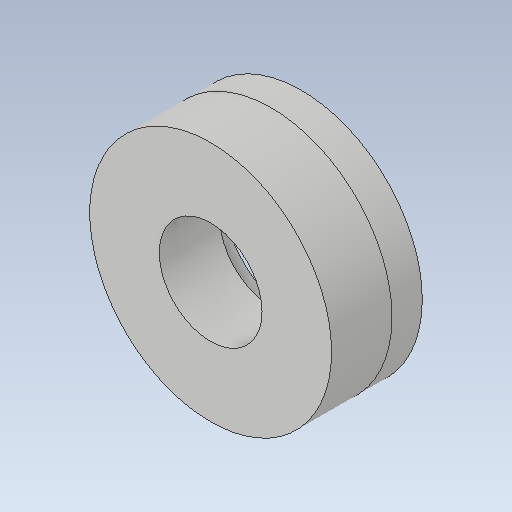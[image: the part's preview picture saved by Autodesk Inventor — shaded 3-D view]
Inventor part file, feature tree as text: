
AUTODESK INVENTOR PART (.ipt)
format: ipt  version: 2020 (Build 240168000, 168)  size: 116,736 bytes
history: native  units: mm
features: other x2, extrude x2, sketch x2
ambient origin geometry x8: Origin, YZ Plane, XZ Plane, XY Plane, X Axis, Y Axis, Z Axis, Center Point
bodies: Body1 (feature_tree), Body2 (feature_tree)
feature tree (6):
  other  "Твердое тело1"
  extrude  "Выдавливание1"  Depth=40.0mm
  extrude  "Выдавливание2"  Depth=26.9mm
  sketch  "Эскиз1"
  sketch  "Эскиз2"
  other  "Твердое тело2"
